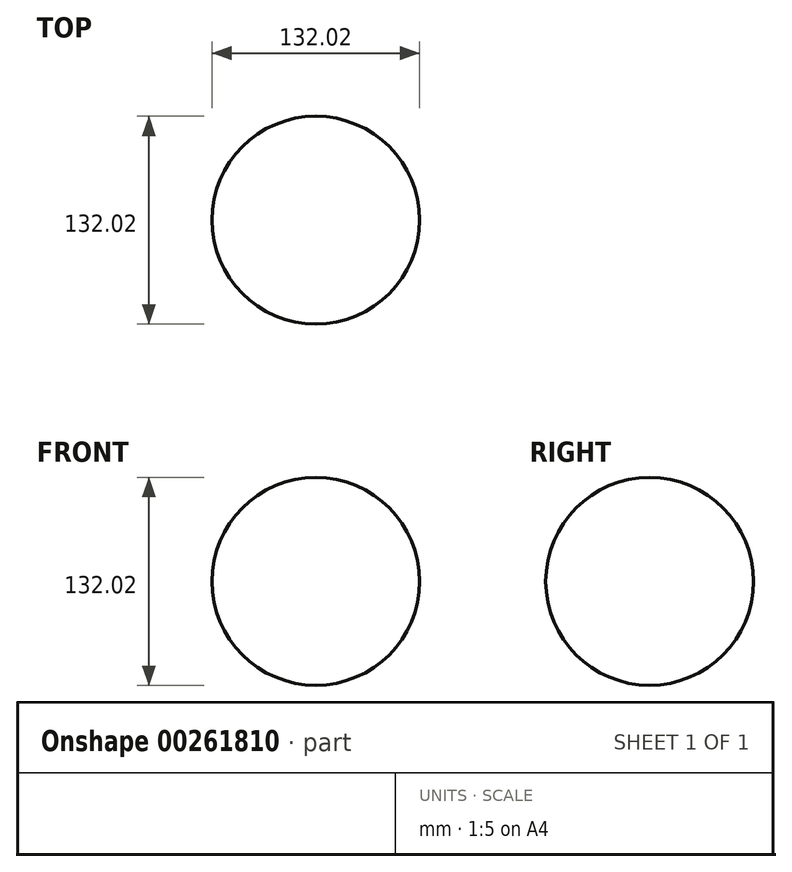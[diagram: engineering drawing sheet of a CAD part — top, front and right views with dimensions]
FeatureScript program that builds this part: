
annotation { "Feature Type Name" : "Feature", "Feature Type Description" : "" }
export const myFeature = defineFeature(function(context is Context, id is Id, definition is map)
    precondition{}
    {
        {
            var Q0;
            Q0=qCreatedBy(makeId("Front.planeOp"),FACE);
            var sketch = newSketch(context, id + "F0", { "sketchPlane" : qUnion([Q0])});
            skLineSegment(sketch, "E0", {"start": v(0, 66) * mm, "end": v(0, -69.79) * mm, "construction": true});
            skArc(sketch, "E1", {"start": v(0, 66) * mm, "mid": v(-66, 0) * mm, "end": v(0, -66) * mm});
            skSolve(sketch);
        }
        {
            var Q0;
            Q0=sQuery(id+"F0.wireOp",EDGE,"E1");
            var Q1;
            Q1=sQuery(id+"F0.wireOp",EDGE,"E0");
            revolve(context, id + "F1", {"bodyType" : ToolBodyType.SURFACE, "surfaceEntities" : qUnion([Q0]), "axis" : qUnion([Q1]), "revolveType" : RevolveType.FULL});
        }
    });
